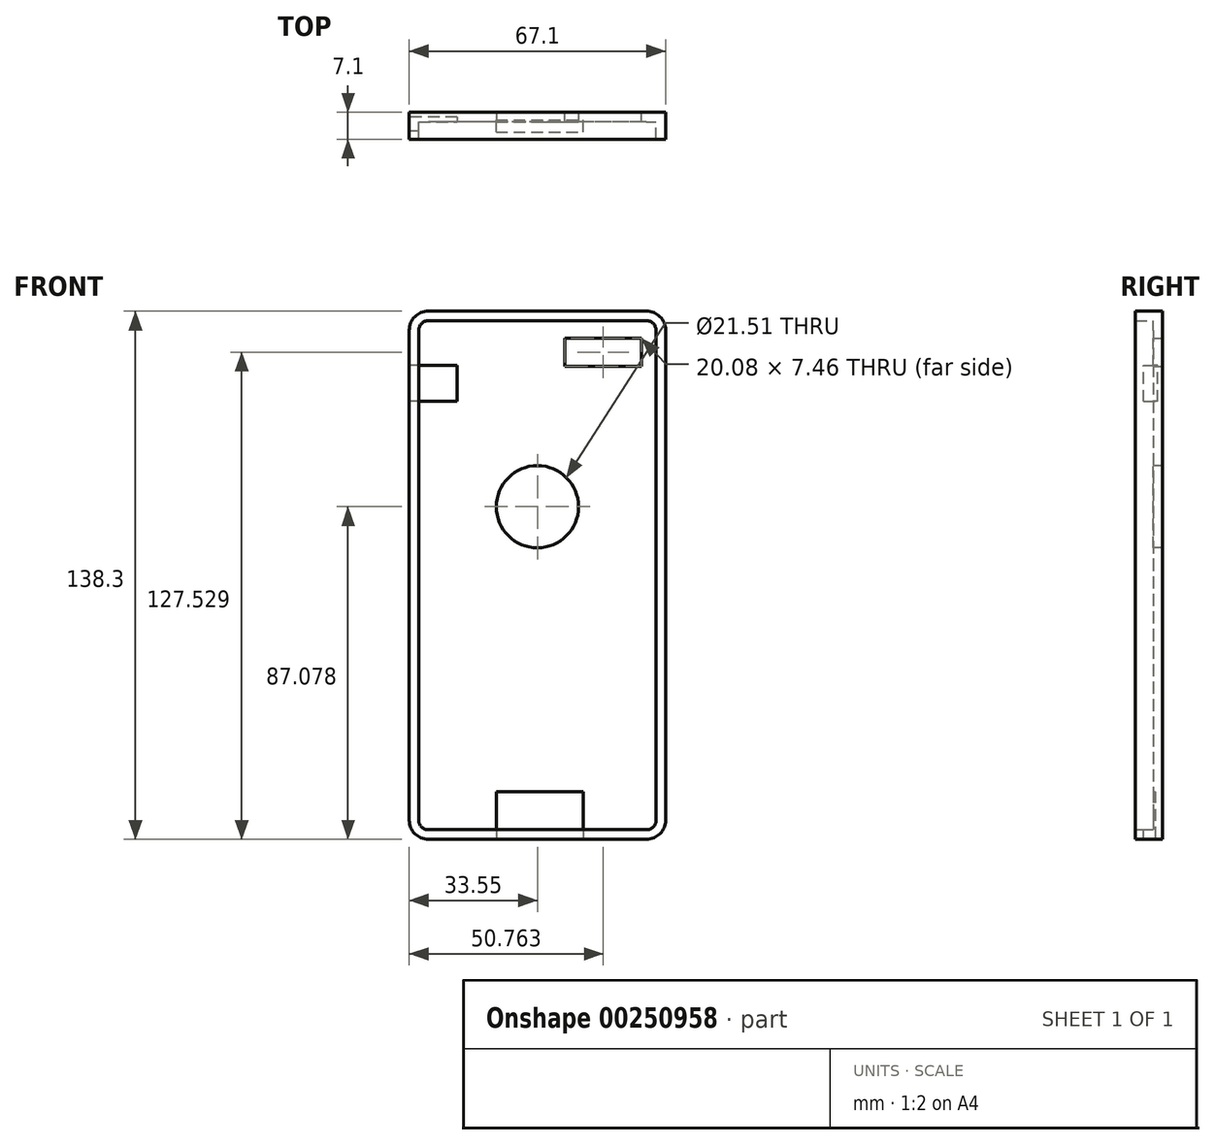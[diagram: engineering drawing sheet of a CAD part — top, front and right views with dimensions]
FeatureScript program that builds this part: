
annotation { "Feature Type Name" : "Feature", "Feature Type Description" : "" }
export const myFeature = defineFeature(function(context is Context, id is Id, definition is map)
    precondition{}
    {
        {
            var Q0;
            Q0=qCreatedBy(makeId("Front.planeOp"),FACE);
            var sketch = newSketch(context, id + "F0", { "sketchPlane" : qUnion([Q0])});
            skLineSegment(sketch, "E0.bottom", {"start": v(33.55, 65.71) * mm, "end": v(-33.55, 65.71) * mm});
            skLineSegment(sketch, "E0.top", {"start": v(33.55, -72.59) * mm, "end": v(-33.55, -72.59) * mm});
            skLineSegment(sketch, "E0.left", {"start": v(33.55, 65.71) * mm, "end": v(33.55, -72.59) * mm});
            skLineSegment(sketch, "E0.right", {"start": v(-33.55, 65.71) * mm, "end": v(-33.55, -72.59) * mm});
            skPoint(sketch, "E0.middle", {"position": v(0, -3.44) * mm});
            skSolve(sketch);
        }
        {
            var Q0;
            Q0=makeQuery(id+"F0.imprint","IMPRINT",FACE,{"disambiguationData":[TD([[makeQuery(id+"F0.imprint","IMPRINT",EDGE,{"derivedFrom":sQuery(id+"F0.wireOp",EDGE,"E0.bottom")}),1.0]])]});
            extrude(context, id + "F1", {"entities" : qUnion([Q0]), "endBound" : BoundingType.SYMMETRIC, "depth" : 7.1 * mm});
        }
        {
            var Q0;
            {var subQ0=sQuery(id+"F0.wireOp",EDGE,"E0.left");var subQ1=sQuery(id+"F0.wireOp",EDGE,"E0.bottom");Q0=makeQuery(id+"FgSe9o79wxvxA3Q_1.boolean.opBoolean","MERGE",EDGE,{"derivedFrom":[makeQuery(id+"F1.opExtrude","SWEPT_EDGE",EDGE,{"disambiguationData":[OSD([subQ1,subQ0])]}),makeQuery(id+"FgSe9o79wxvxA3Q_1.opExtrude","SWEPT_EDGE",EDGE,{"disambiguationData":[OSD([subQ1,subQ0])]})]});}
            var Q1;
            {var subQ0=sQuery(id+"F0.wireOp",EDGE,"E0.left");var subQ1=sQuery(id+"F0.wireOp",EDGE,"E0.top");Q1=makeQuery(id+"FgSe9o79wxvxA3Q_1.boolean.opBoolean","MERGE",EDGE,{"derivedFrom":[makeQuery(id+"F1.opExtrude","SWEPT_EDGE",EDGE,{"disambiguationData":[OSD([subQ1,subQ0])]}),makeQuery(id+"FgSe9o79wxvxA3Q_1.opExtrude","SWEPT_EDGE",EDGE,{"disambiguationData":[OSD([subQ1,subQ0])]})]});}
            var Q2;
            {var subQ0=sQuery(id+"F0.wireOp",EDGE,"E0.right");var subQ1=sQuery(id+"F0.wireOp",EDGE,"E0.bottom");Q2=makeQuery(id+"FgSe9o79wxvxA3Q_1.boolean.opBoolean","MERGE",EDGE,{"derivedFrom":[makeQuery(id+"F1.opExtrude","SWEPT_EDGE",EDGE,{"disambiguationData":[OSD([subQ1,subQ0])]}),makeQuery(id+"FgSe9o79wxvxA3Q_1.opExtrude","SWEPT_EDGE",EDGE,{"disambiguationData":[OSD([subQ1,subQ0])]})]});}
            var Q3;
            {var subQ0=sQuery(id+"F0.wireOp",EDGE,"E0.right");var subQ1=sQuery(id+"F0.wireOp",EDGE,"E0.top");Q3=makeQuery(id+"FgSe9o79wxvxA3Q_1.boolean.opBoolean","MERGE",EDGE,{"derivedFrom":[makeQuery(id+"F1.opExtrude","SWEPT_EDGE",EDGE,{"disambiguationData":[OSD([subQ1,subQ0])]}),makeQuery(id+"FgSe9o79wxvxA3Q_1.opExtrude","SWEPT_EDGE",EDGE,{"disambiguationData":[OSD([subQ1,subQ0])]})]});}
            fillet(context, id + "F2", {"entities" : qUnion([Q0, Q1, Q2, Q3]), "radius" : 5 * mm, "tangentPropagation" : true, "allowEdgeOverflow" : false});
        }
        {
            var Q0;
            Q0=makeQuery(id+"F1.opExtrude","CAP_FACE",FACE,{"disambiguationData":[OSD([sQuery(id+"F0.wireOp",EDGE,"E0.bottom"),sQuery(id+"F0.wireOp",EDGE,"E0.top"),sQuery(id+"F0.wireOp",EDGE,"E0.left"),sQuery(id+"F0.wireOp",EDGE,"E0.right")])],"isStart":false});
            shell(context, id + "F3", {"entities" : qUnion([Q0]), "thickness" : 2.5 * mm});
        }
        {
            var Q0;
            Q0=makeQuery(id+"F3.opShell","OFFSET_FACE",FACE,{"disambiguationData":[OSD([sQuery(id+"F0.wireOp",EDGE,"E0.bottom"),sQuery(id+"F0.wireOp",EDGE,"E0.top"),sQuery(id+"F0.wireOp",EDGE,"E0.left"),sQuery(id+"F0.wireOp",EDGE,"E0.right")])]});
            var sketch = newSketch(context, id + "F4", { "sketchPlane" : qUnion([Q0])});
            skLineSegment(sketch, "E1.bottom", {"start": v(7.17, 58.67) * mm, "end": v(27.25, 58.67) * mm});
            skLineSegment(sketch, "E1.top", {"start": v(7.17, 51.2) * mm, "end": v(27.25, 51.2) * mm});
            skLineSegment(sketch, "E1.left", {"start": v(7.17, 58.67) * mm, "end": v(7.17, 51.2) * mm});
            skLineSegment(sketch, "E1.right", {"start": v(27.25, 58.67) * mm, "end": v(27.25, 51.2) * mm});
            skSolve(sketch);
        }
        {
            var Q0;
            Q0=makeQuery(id+"F4.imprint","IMPRINT",FACE,{"disambiguationData":[TD([[makeQuery(id+"F4.imprint","IMPRINT",EDGE,{"derivedFrom":sQuery(id+"F4.wireOp",EDGE,"E1.bottom")}),-1.0]])]});
            extrude(context, id + "F5", {"entities" : qUnion([Q0]), "operationType" : NewBodyOperationType.REMOVE, "endBound" : BoundingType.SYMMETRIC, "depth" : 25 * mm});
        }
        {
            var Q0;
            Q0=makeQuery(id+"F1.opExtrude","SWEPT_FACE",FACE,{"disambiguationData":[OSD([sQuery(id+"F0.wireOp",EDGE,"E0.top")])]});
            var sketch = newSketch(context, id + "F6", { "sketchPlane" : qUnion([Q0])});
            skLineSegment(sketch, "E2.bottom", {"start": v(-10.8, 1.61) * mm, "end": v(11.96, 1.61) * mm});
            skLineSegment(sketch, "E2.top", {"start": v(-10.8, -1.56) * mm, "end": v(11.96, -1.56) * mm});
            skLineSegment(sketch, "E2.left", {"start": v(-10.8, 1.61) * mm, "end": v(-10.8, -1.56) * mm});
            skLineSegment(sketch, "E2.right", {"start": v(11.96, 1.61) * mm, "end": v(11.96, -1.56) * mm});
            skSolve(sketch);
        }
        {
            var Q0;
            Q0=makeQuery(id+"F3.opShell","OFFSET_FACE",FACE,{"disambiguationData":[OSD([sQuery(id+"F0.wireOp",EDGE,"E0.bottom"),sQuery(id+"F0.wireOp",EDGE,"E0.top"),sQuery(id+"F0.wireOp",EDGE,"E0.left"),sQuery(id+"F0.wireOp",EDGE,"E0.right")])]});
            var sketch = newSketch(context, id + "F7", { "sketchPlane" : qUnion([Q0])});
            skCircle(sketch, "E3", {"center": v(0, 14.49) * mm, "radius": 10.75 * mm});
            skSolve(sketch);
        }
        {
            var Q0;
            Q0=makeQuery(id+"F7.imprint","IMPRINT",FACE,{"disambiguationData":[TD([[makeQuery(id+"F7.imprint","IMPRINT",EDGE,{"derivedFrom":sQuery(id+"F7.wireOp",EDGE,"E3")}),1.0]])]});
            extrude(context, id + "F8", {"entities" : qUnion([Q0]), "operationType" : NewBodyOperationType.REMOVE, "endBound" : BoundingType.SYMMETRIC, "oppositeDirection" : true, "depth" : 25 * mm});
        }
        {
            var Q0;
            Q0=makeQuery(id+"F6.imprint","IMPRINT",FACE,{"disambiguationData":[TD([[makeQuery(id+"F6.imprint","IMPRINT",EDGE,{"derivedFrom":sQuery(id+"F6.wireOp",EDGE,"E2.bottom")}),-1.0]])]});
            extrude(context, id + "F9", {"entities" : qUnion([Q0]), "operationType" : NewBodyOperationType.REMOVE, "endBound" : BoundingType.SYMMETRIC, "oppositeDirection" : true, "depth" : 25 * mm});
        }
        {
            var Q0;
            Q0=makeQuery(id+"F1.opExtrude","SWEPT_FACE",FACE,{"disambiguationData":[OSD([sQuery(id+"F0.wireOp",EDGE,"E0.right")])]});
            var sketch = newSketch(context, id + "F10", { "sketchPlane" : qUnion([Q0])});
            skLineSegment(sketch, "E4.bottom", {"start": v(-2.28, 51.54) * mm, "end": v(1.42, 51.54) * mm});
            skLineSegment(sketch, "E4.top", {"start": v(-2.28, 42.09) * mm, "end": v(1.42, 42.09) * mm});
            skLineSegment(sketch, "E4.left", {"start": v(-2.28, 51.54) * mm, "end": v(-2.28, 42.09) * mm});
            skLineSegment(sketch, "E4.right", {"start": v(1.42, 51.54) * mm, "end": v(1.42, 42.09) * mm});
            skSolve(sketch);
        }
        {
            var Q0;
            Q0=makeQuery(id+"F10.imprint","IMPRINT",FACE,{"disambiguationData":[TD([[makeQuery(id+"F10.imprint","IMPRINT",EDGE,{"derivedFrom":sQuery(id+"F10.wireOp",EDGE,"E4.bottom")}),-1.0]])]});
            extrude(context, id + "F11", {"entities" : qUnion([Q0]), "operationType" : NewBodyOperationType.REMOVE, "endBound" : BoundingType.SYMMETRIC, "oppositeDirection" : true, "depth" : 25 * mm});
        }
    });
